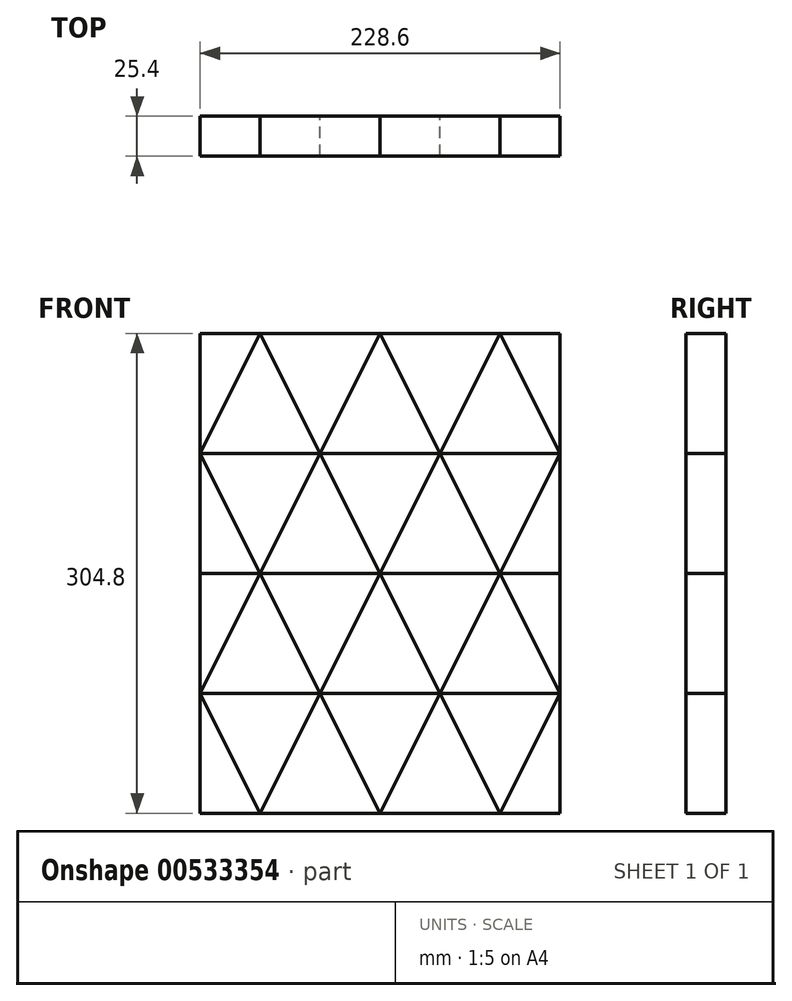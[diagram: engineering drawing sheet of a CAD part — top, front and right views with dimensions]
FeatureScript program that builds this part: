
annotation { "Feature Type Name" : "Feature", "Feature Type Description" : "" }
export const myFeature = defineFeature(function(context is Context, id is Id, definition is map)
    precondition{}
    {
        {
            var Q0;
            Q0=qCreatedBy(makeId("Front.planeOp"),FACE);
            var sketch = newSketch(context, id + "F0", { "sketchPlane" : qUnion([Q0])});
            skLineSegment(sketch, "E0.bottom", {"start": v(-114.3, 152.4) * mm, "end": v(114.3, 152.4) * mm});
            skLineSegment(sketch, "E0.top", {"start": v(-114.3, -152.4) * mm, "end": v(114.3, -152.4) * mm});
            skLineSegment(sketch, "E0.left", {"start": v(-114.3, 152.4) * mm, "end": v(-114.3, -152.4) * mm});
            skLineSegment(sketch, "E0.right", {"start": v(114.3, 152.4) * mm, "end": v(114.3, -152.4) * mm});
            skPoint(sketch, "E0.middle", {"position": v(0, 0) * mm});
            skLineSegment(sketch, "E1", {"start": v(-114.3, 76.2) * mm, "end": v(114.3, 76.2) * mm});
            skLineSegment(sketch, "E2.0", {"start": v(-114.3, -76.2) * mm, "end": v(114.3, -76.2) * mm});
            skLineSegment(sketch, "E3.0", {"start": v(-114.3, 0) * mm, "end": v(114.3, 0) * mm});
            skLineSegment(sketch, "E4", {"start": v(-114.3, 76.2) * mm, "end": v(-76.2, 152.4) * mm});
            skLineSegment(sketch, "E5", {"start": v(-76.2, 152.4) * mm, "end": v(-38.1, 76.2) * mm});
            skLineSegment(sketch, "E6", {"start": v(-38.1, 76.2) * mm, "end": v(0, 152.4) * mm});
            skLineSegment(sketch, "E7", {"start": v(0, 152.4) * mm, "end": v(38.1, 76.2) * mm});
            skLineSegment(sketch, "E8", {"start": v(38.1, 76.2) * mm, "end": v(76.2, 152.4) * mm});
            skLineSegment(sketch, "E9", {"start": v(76.2, 152.4) * mm, "end": v(114.3, 76.2) * mm});
            skLineSegment(sketch, "E10.MirrorCS", {"start": v(-114.3, 76.2) * mm, "end": v(-76.2, 0) * mm});
            skLineSegment(sketch, "E11.MirrorCS", {"start": v(-76.2, 0) * mm, "end": v(-38.1, 76.2) * mm});
            skLineSegment(sketch, "E12.MirrorCS", {"start": v(-38.1, 76.2) * mm, "end": v(0, 0) * mm});
            skLineSegment(sketch, "E13.MirrorCS", {"start": v(0, 0) * mm, "end": v(38.1, 76.2) * mm});
            skLineSegment(sketch, "E14.MirrorCS", {"start": v(38.1, 76.2) * mm, "end": v(76.2, 0) * mm});
            skLineSegment(sketch, "E15.MirrorCS", {"start": v(76.2, 0) * mm, "end": v(114.3, 76.2) * mm});
            skLineSegment(sketch, "E16.MirrorCS", {"start": v(-114.3, -76.2) * mm, "end": v(-76.2, 0) * mm});
            skLineSegment(sketch, "E17.MirrorCS", {"start": v(-76.2, 0) * mm, "end": v(-38.1, -76.2) * mm});
            skLineSegment(sketch, "E18.MirrorCS", {"start": v(-38.1, -76.2) * mm, "end": v(0, 0) * mm});
            skLineSegment(sketch, "E19.MirrorCS", {"start": v(0, 0) * mm, "end": v(38.1, -76.2) * mm});
            skLineSegment(sketch, "E20.MirrorCS", {"start": v(38.1, -76.2) * mm, "end": v(76.2, 0) * mm});
            skLineSegment(sketch, "E21.MirrorCS", {"start": v(76.2, 0) * mm, "end": v(114.3, -76.2) * mm});
            skLineSegment(sketch, "E22.MirrorCS", {"start": v(76.2, -152.4) * mm, "end": v(114.3, -76.2) * mm});
            skLineSegment(sketch, "E23.MirrorCS", {"start": v(38.1, -76.2) * mm, "end": v(76.2, -152.4) * mm});
            skLineSegment(sketch, "E24.MirrorCS", {"start": v(0, -152.4) * mm, "end": v(38.1, -76.2) * mm});
            skLineSegment(sketch, "E25.MirrorCS", {"start": v(-38.1, -76.2) * mm, "end": v(0, -152.4) * mm});
            skLineSegment(sketch, "E26.MirrorCS", {"start": v(-76.2, -152.4) * mm, "end": v(-38.1, -76.2) * mm});
            skLineSegment(sketch, "E27.MirrorCS", {"start": v(-114.3, -76.2) * mm, "end": v(-76.2, -152.4) * mm});
            skSolve(sketch);
        }
        {
            var Q0;
            {var subQ3=sQuery(id+"F0.wireOp",EDGE,"E4");Q0=makeQuery(id+"F0.imprint","IMPRINT",FACE,{"disambiguationData":[TD([[makeQuery(id+"F0.imprint","IMPRINT",EDGE,{"derivedFrom":subQ3}),1.0]])]});}
            var Q1;
            {var subQ0=sQuery(id+"F0.wireOp",EDGE,"E5");Q1=makeQuery(id+"F0.imprint","IMPRINT",FACE,{"disambiguationData":[TD([[makeQuery(id+"F0.imprint","IMPRINT",EDGE,{"derivedFrom":subQ0}),1.0]])]});}
            var Q2;
            {var subQ0=sQuery(id+"F0.wireOp",EDGE,"E7");Q2=makeQuery(id+"F0.imprint","IMPRINT",FACE,{"disambiguationData":[TD([[makeQuery(id+"F0.imprint","IMPRINT",EDGE,{"derivedFrom":subQ0}),1.0]])]});}
            var Q3;
            {var subQ3=sQuery(id+"F0.wireOp",EDGE,"E9");Q3=makeQuery(id+"F0.imprint","IMPRINT",FACE,{"disambiguationData":[TD([[makeQuery(id+"F0.imprint","IMPRINT",EDGE,{"derivedFrom":subQ3}),1.0]])]});}
            var Q4;
            {var subQ0=sQuery(id+"F0.wireOp",EDGE,"E15.MirrorCS");Q4=makeQuery(id+"F0.imprint","IMPRINT",FACE,{"disambiguationData":[TD([[makeQuery(id+"F0.imprint","IMPRINT",EDGE,{"derivedFrom":subQ0}),-1.0]])]});}
            var Q5;
            {var subQ0=sQuery(id+"F0.wireOp",EDGE,"E13.MirrorCS");Q5=makeQuery(id+"F0.imprint","IMPRINT",FACE,{"disambiguationData":[TD([[makeQuery(id+"F0.imprint","IMPRINT",EDGE,{"derivedFrom":subQ0}),-1.0]])]});}
            var Q6;
            {var subQ0=sQuery(id+"F0.wireOp",EDGE,"E11.MirrorCS");Q6=makeQuery(id+"F0.imprint","IMPRINT",FACE,{"disambiguationData":[TD([[makeQuery(id+"F0.imprint","IMPRINT",EDGE,{"derivedFrom":subQ0}),-1.0]])]});}
            var Q7;
            {var subQ0=sQuery(id+"F0.wireOp",EDGE,"E10.MirrorCS");Q7=makeQuery(id+"F0.imprint","IMPRINT",FACE,{"disambiguationData":[TD([[makeQuery(id+"F0.imprint","IMPRINT",EDGE,{"derivedFrom":subQ0}),-1.0]])]});}
            var Q8;
            {var subQ0=sQuery(id+"F0.wireOp",EDGE,"E16.MirrorCS");Q8=makeQuery(id+"F0.imprint","IMPRINT",FACE,{"disambiguationData":[TD([[makeQuery(id+"F0.imprint","IMPRINT",EDGE,{"derivedFrom":subQ0}),-1.0]])]});}
            var Q9;
            {var subQ0=sQuery(id+"F0.wireOp",EDGE,"E18.MirrorCS");Q9=makeQuery(id+"F0.imprint","IMPRINT",FACE,{"disambiguationData":[TD([[makeQuery(id+"F0.imprint","IMPRINT",EDGE,{"derivedFrom":subQ0}),-1.0]])]});}
            var Q10;
            {var subQ2=sQuery(id+"F0.wireOp",EDGE,"E20.MirrorCS");Q10=makeQuery(id+"F0.imprint","IMPRINT",FACE,{"disambiguationData":[TD([[makeQuery(id+"F0.imprint","IMPRINT",EDGE,{"derivedFrom":subQ2}),-1.0]])]});}
            var Q11;
            {var subQ3=sQuery(id+"F0.wireOp",EDGE,"E22.MirrorCS");Q11=makeQuery(id+"F0.imprint","IMPRINT",FACE,{"disambiguationData":[TD([[makeQuery(id+"F0.imprint","IMPRINT",EDGE,{"derivedFrom":subQ3}),-1.0]])]});}
            var Q12;
            {var subQ0=sQuery(id+"F0.wireOp",EDGE,"E23.MirrorCS");Q12=makeQuery(id+"F0.imprint","IMPRINT",FACE,{"disambiguationData":[TD([[makeQuery(id+"F0.imprint","IMPRINT",EDGE,{"derivedFrom":subQ0}),-1.0]])]});}
            var Q13;
            {var subQ0=sQuery(id+"F0.wireOp",EDGE,"E25.MirrorCS");Q13=makeQuery(id+"F0.imprint","IMPRINT",FACE,{"disambiguationData":[TD([[makeQuery(id+"F0.imprint","IMPRINT",EDGE,{"derivedFrom":subQ0}),-1.0]])]});}
            var Q14;
            {var subQ3=sQuery(id+"F0.wireOp",EDGE,"E27.MirrorCS");Q14=makeQuery(id+"F0.imprint","IMPRINT",FACE,{"disambiguationData":[TD([[makeQuery(id+"F0.imprint","IMPRINT",EDGE,{"derivedFrom":subQ3}),-1.0]])]});}
            extrude(context, id + "F1", {"entities" : qUnion([Q0, Q1, Q2, Q3, Q4, Q5, Q6, Q7, Q8, Q9, Q10, Q11, Q12, Q13, Q14]), "depth" : 25.4 * mm, "offsetDistance" : 25.4 * mm});
        }
        {
            var Q0;
            {var subQ0=sQuery(id+"F0.wireOp",EDGE,"E4");Q0=makeQuery(id+"F0.imprint","IMPRINT",FACE,{"disambiguationData":[TD([[makeQuery(id+"F0.imprint","IMPRINT",EDGE,{"derivedFrom":subQ0}),-1.0]])]});}
            var Q1;
            {var subQ0=sQuery(id+"F0.wireOp",EDGE,"E6");Q1=makeQuery(id+"F0.imprint","IMPRINT",FACE,{"disambiguationData":[TD([[makeQuery(id+"F0.imprint","IMPRINT",EDGE,{"derivedFrom":subQ0}),-1.0]])]});}
            var Q2;
            {var subQ2=sQuery(id+"F0.wireOp",EDGE,"E8");Q2=makeQuery(id+"F0.imprint","IMPRINT",FACE,{"disambiguationData":[TD([[makeQuery(id+"F0.imprint","IMPRINT",EDGE,{"derivedFrom":subQ2}),-1.0]])]});}
            var Q3;
            {var subQ0=sQuery(id+"F0.wireOp",EDGE,"E21.MirrorCS");Q3=makeQuery(id+"F0.imprint","IMPRINT",FACE,{"disambiguationData":[TD([[makeQuery(id+"F0.imprint","IMPRINT",EDGE,{"derivedFrom":subQ0}),1.0]])]});}
            var Q4;
            {var subQ0=sQuery(id+"F0.wireOp",EDGE,"E19.MirrorCS");Q4=makeQuery(id+"F0.imprint","IMPRINT",FACE,{"disambiguationData":[TD([[makeQuery(id+"F0.imprint","IMPRINT",EDGE,{"derivedFrom":subQ0}),1.0]])]});}
            var Q5;
            {var subQ0=sQuery(id+"F0.wireOp",EDGE,"E17.MirrorCS");Q5=makeQuery(id+"F0.imprint","IMPRINT",FACE,{"disambiguationData":[TD([[makeQuery(id+"F0.imprint","IMPRINT",EDGE,{"derivedFrom":subQ0}),1.0]])]});}
            var Q6;
            {var subQ0=sQuery(id+"F0.wireOp",EDGE,"E16.MirrorCS");Q6=makeQuery(id+"F0.imprint","IMPRINT",FACE,{"disambiguationData":[TD([[makeQuery(id+"F0.imprint","IMPRINT",EDGE,{"derivedFrom":subQ0}),1.0]])]});}
            var Q7;
            {var subQ2=sQuery(id+"F0.wireOp",EDGE,"E26.MirrorCS");Q7=makeQuery(id+"F0.imprint","IMPRINT",FACE,{"disambiguationData":[TD([[makeQuery(id+"F0.imprint","IMPRINT",EDGE,{"derivedFrom":subQ2}),1.0]])]});}
            var Q8;
            {var subQ2=sQuery(id+"F0.wireOp",EDGE,"E24.MirrorCS");Q8=makeQuery(id+"F0.imprint","IMPRINT",FACE,{"disambiguationData":[TD([[makeQuery(id+"F0.imprint","IMPRINT",EDGE,{"derivedFrom":subQ2}),1.0]])]});}
            var Q9;
            {var subQ0=sQuery(id+"F0.wireOp",EDGE,"E22.MirrorCS");Q9=makeQuery(id+"F0.imprint","IMPRINT",FACE,{"disambiguationData":[TD([[makeQuery(id+"F0.imprint","IMPRINT",EDGE,{"derivedFrom":subQ0}),1.0]])]});}
            extrude(context, id + "F2", {"entities" : qUnion([Q0, Q1, Q2, Q3, Q4, Q5, Q6, Q7, Q8, Q9]), "depth" : 25.4 * mm, "offsetDistance" : 25.4 * mm});
        }
        {
            var Q0;
            {var subQ0=sQuery(id+"F0.wireOp",EDGE,"E10.MirrorCS");Q0=makeQuery(id+"F0.imprint","IMPRINT",FACE,{"disambiguationData":[TD([[makeQuery(id+"F0.imprint","IMPRINT",EDGE,{"derivedFrom":subQ0}),1.0]])]});}
            var Q1;
            {var subQ0=sQuery(id+"F0.wireOp",EDGE,"E12.MirrorCS");Q1=makeQuery(id+"F0.imprint","IMPRINT",FACE,{"disambiguationData":[TD([[makeQuery(id+"F0.imprint","IMPRINT",EDGE,{"derivedFrom":subQ0}),1.0]])]});}
            var Q2;
            {var subQ2=sQuery(id+"F0.wireOp",EDGE,"E14.MirrorCS");Q2=makeQuery(id+"F0.imprint","IMPRINT",FACE,{"disambiguationData":[TD([[makeQuery(id+"F0.imprint","IMPRINT",EDGE,{"derivedFrom":subQ2}),1.0]])]});}
            extrude(context, id + "F3", {"entities" : qUnion([Q0, Q1, Q2]), "depth" : 25.4 * mm, "offsetDistance" : 25.4 * mm});
        }
    });
